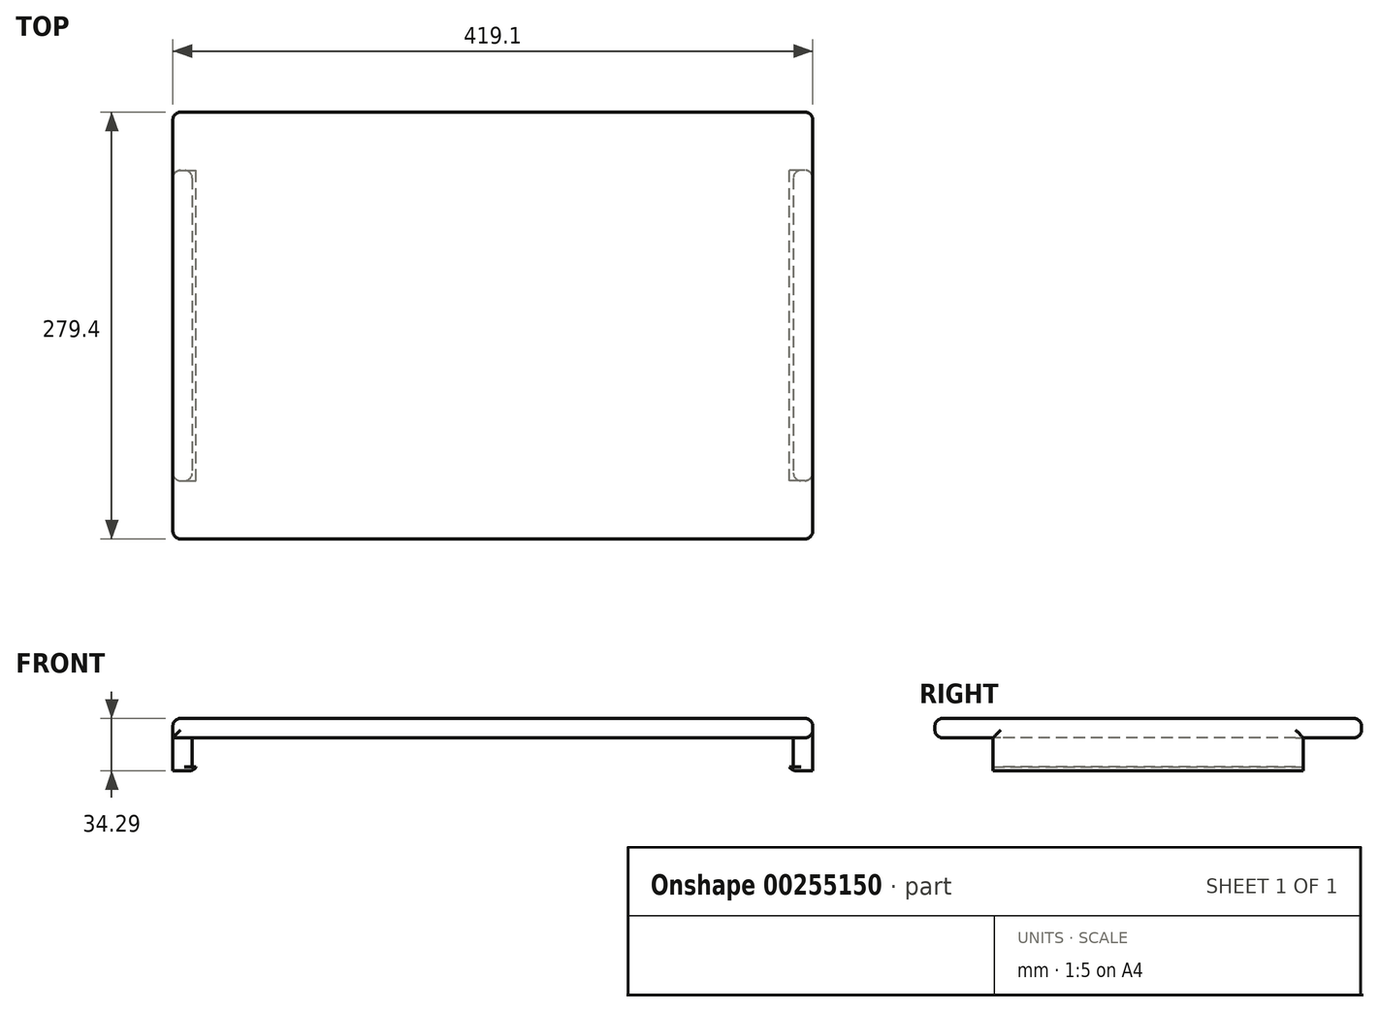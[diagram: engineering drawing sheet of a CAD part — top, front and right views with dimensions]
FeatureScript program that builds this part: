
annotation { "Feature Type Name" : "Feature", "Feature Type Description" : "" }
export const myFeature = defineFeature(function(context is Context, id is Id, definition is map)
    precondition{}
    {
        {
            var Q0;
            Q0=qCreatedBy(makeId("Top.planeOp"),FACE);
            var sketch = newSketch(context, id + "F0", { "sketchPlane" : qUnion([Q0])});
            skLineSegment(sketch, "E0.bottom", {"start": v(-209.55, 139.7) * mm, "end": v(209.55, 139.7) * mm});
            skLineSegment(sketch, "E0.top", {"start": v(-209.55, -139.7) * mm, "end": v(209.55, -139.7) * mm});
            skLineSegment(sketch, "E0.left", {"start": v(-209.55, 139.7) * mm, "end": v(-209.55, -139.7) * mm});
            skLineSegment(sketch, "E0.right", {"start": v(209.55, 139.7) * mm, "end": v(209.55, -139.7) * mm});
            skLineSegment(sketch, "E1.bottom", {"start": v(-209.55, 101.6) * mm, "end": v(-196.85, 101.6) * mm});
            skLineSegment(sketch, "E1.top", {"start": v(-209.55, -101.6) * mm, "end": v(-196.85, -101.6) * mm});
            skLineSegment(sketch, "E1.left", {"start": v(-209.55, 101.6) * mm, "end": v(-209.55, -101.6) * mm});
            skLineSegment(sketch, "E1.right", {"start": v(-196.85, 101.6) * mm, "end": v(-196.85, -101.6) * mm});
            skLineSegment(sketch, "E2.bottom", {"start": v(209.55, 101.6) * mm, "end": v(196.85, 101.6) * mm});
            skLineSegment(sketch, "E2.top", {"start": v(209.55, -101.6) * mm, "end": v(196.85, -101.6) * mm});
            skLineSegment(sketch, "E2.left", {"start": v(209.55, 101.6) * mm, "end": v(209.55, -101.6) * mm});
            skLineSegment(sketch, "E2.right", {"start": v(196.85, 101.6) * mm, "end": v(196.85, -101.6) * mm});
            skLineSegment(sketch, "E3.bottom", {"start": v(-76.2, -139.7) * mm, "end": v(76.2, -139.7) * mm});
            skLineSegment(sketch, "E3.top", {"start": v(-76.2, -127) * mm, "end": v(76.2, -127) * mm});
            skLineSegment(sketch, "E3.left", {"start": v(-76.2, -139.7) * mm, "end": v(-76.2, -127) * mm});
            skLineSegment(sketch, "E3.right", {"start": v(76.2, -139.7) * mm, "end": v(76.2, -127) * mm});
            skSolve(sketch);
        }
        {
            var Q0;
            Q0 = qSketchRegion(id + "F0", true);
            extrude(context, id + "F1", {"entities" : qUnion([Q0]), "depth" : 12.7 * mm});
        }
        {
            var Q0;
            Q0=makeQuery(id+"F0.imprint","IMPRINT",FACE,{"disambiguationData":[TD([[makeQuery(id+"F0.imprint","IMPRINT",EDGE,{"derivedFrom":sQuery(id+"F0.wireOp",EDGE,"E1.bottom")}),-1.0]])]});
            var Q1;
            Q1=makeQuery(id+"F0.imprint","IMPRINT",FACE,{"disambiguationData":[TD([[makeQuery(id+"F0.imprint","IMPRINT",EDGE,{"derivedFrom":sQuery(id+"F0.wireOp",EDGE,"E2.bottom")}),1.0]])]});
            var Q2;
            Q2=makeQuery(id+"F0.imprint","IMPRINT",FACE,{"disambiguationData":[TD([[makeQuery(id+"F0.imprint","IMPRINT",EDGE,{"derivedFrom":sQuery(id+"F0.wireOp",EDGE,"E3.bottom")}),1.0]])]});
            extrude(context, id + "F2", {"entities" : qUnion([Q0, Q1, Q2]), "operationType" : NewBodyOperationType.ADD, "oppositeDirection" : true, "depth" : 19.05 * mm});
        }
        {
            var Q0;
            Q0=makeQuery(id+"F1.opExtrude","SWEPT_EDGE",EDGE,{"disambiguationData":[OSD([sQuery(id+"F0.wireOp",EDGE,"E0.bottom"),sQuery(id+"F0.wireOp",EDGE,"E0.right")])]});
            var Q1;
            Q1=makeQuery(id+"F1.opExtrude","CAP_EDGE",EDGE,{"disambiguationData":[OSD([sQuery(id+"F0.wireOp",EDGE,"E0.right"),sQuery(id+"F0.wireOp",EDGE,"E2.left")])],"isStart":false});
            var Q2;
            Q2=makeQuery(id+"F1.opExtrude","CAP_EDGE",EDGE,{"disambiguationData":[OSD([sQuery(id+"F0.wireOp",EDGE,"E0.bottom")])],"isStart":false});
            var Q3;
            Q3=makeQuery(id+"F1.opExtrude","CAP_EDGE",EDGE,{"disambiguationData":[OSD([sQuery(id+"F0.wireOp",EDGE,"E0.bottom")])],"isStart":true});
            var Q4;
            {var subQ0=sQuery(id+"F0.wireOp",EDGE,"E2.left");var subQ1=sQuery(id+"F0.wireOp",EDGE,"E0.right");var subQ2=sQuery(id+"F0.wireOp",EDGE,"E0.bottom");Q4=makeQuery(id+"F2.boolean.opBoolean","SPLIT",EDGE,{"disambiguationData":[TD([makeQuery(id+"F1.opExtrude","SWEPT_FACE",FACE,{"disambiguationData":[OSD([subQ2])]})])],"derivedFrom":makeQuery(id+"F1.opExtrude","CAP_EDGE",EDGE,{"disambiguationData":[OSD([subQ1,subQ0])],"isStart":true})});}
            var Q5;
            {var subQ0=sQuery(id+"F0.wireOp",EDGE,"E2.left");var subQ1=sQuery(id+"F0.wireOp",EDGE,"E0.right");var subQ2=sQuery(id+"F0.wireOp",EDGE,"E0.top");Q5=makeQuery(id+"F2.boolean.opBoolean","SPLIT",EDGE,{"disambiguationData":[TD([makeQuery(id+"F1.opExtrude","SWEPT_FACE",FACE,{"disambiguationData":[OSD([subQ2])]})])],"derivedFrom":makeQuery(id+"F1.opExtrude","CAP_EDGE",EDGE,{"disambiguationData":[OSD([subQ1,subQ0])],"isStart":true})});}
            var Q6;
            Q6=makeQuery(id+"F1.opExtrude","CAP_EDGE",EDGE,{"disambiguationData":[OSD([sQuery(id+"F0.wireOp",EDGE,"E0.top")])],"isStart":true});
            var Q7;
            Q7=makeQuery(id+"F1.opExtrude","CAP_EDGE",EDGE,{"disambiguationData":[OSD([sQuery(id+"F0.wireOp",EDGE,"E0.top")])],"isStart":false});
            var Q8;
            Q8=makeQuery(id+"F1.opExtrude","SWEPT_EDGE",EDGE,{"disambiguationData":[OSD([sQuery(id+"F0.wireOp",EDGE,"E0.top"),sQuery(id+"F0.wireOp",EDGE,"E0.right")])]});
            var Q9;
            Q9=makeQuery(id+"F1.opExtrude","SWEPT_EDGE",EDGE,{"disambiguationData":[OSD([sQuery(id+"F0.wireOp",EDGE,"E0.top"),sQuery(id+"F0.wireOp",EDGE,"E0.left")])]});
            var Q10;
            Q10=makeQuery(id+"F2.opExtrude","SWEPT_EDGE",EDGE,{"disambiguationData":[OSD([sQuery(id+"F0.wireOp",EDGE,"E0.left"),sQuery(id+"F0.wireOp",EDGE,"E1.top"),sQuery(id+"F0.wireOp",EDGE,"E1.left")])]});
            var Q11;
            Q11=makeQuery(id+"F2.opExtrude","SWEPT_EDGE",EDGE,{"disambiguationData":[OSD([sQuery(id+"F0.wireOp",EDGE,"E0.left"),sQuery(id+"F0.wireOp",EDGE,"E1.bottom"),sQuery(id+"F0.wireOp",EDGE,"E1.left")])]});
            var Q12;
            Q12=makeQuery(id+"F2.opExtrude","SWEPT_EDGE",EDGE,{"disambiguationData":[OSD([sQuery(id+"F0.wireOp",EDGE,"E2.bottom"),sQuery(id+"F0.wireOp",EDGE,"E2.right")])]});
            var Q13;
            Q13=makeQuery(id+"F2.opExtrude","SWEPT_EDGE",EDGE,{"disambiguationData":[OSD([sQuery(id+"F0.wireOp",EDGE,"E0.right"),sQuery(id+"F0.wireOp",EDGE,"E2.bottom"),sQuery(id+"F0.wireOp",EDGE,"E2.left")])]});
            var Q14;
            {var subQ0=sQuery(id+"F0.wireOp",EDGE,"E1.left");var subQ1=sQuery(id+"F0.wireOp",EDGE,"E0.left");var subQ2=sQuery(id+"F0.wireOp",EDGE,"E0.bottom");Q14=makeQuery(id+"F2.boolean.opBoolean","SPLIT",EDGE,{"disambiguationData":[TD([makeQuery(id+"F1.opExtrude","SWEPT_FACE",FACE,{"disambiguationData":[OSD([subQ2])]})])],"derivedFrom":makeQuery(id+"F1.opExtrude","CAP_EDGE",EDGE,{"disambiguationData":[OSD([subQ1,subQ0])],"isStart":true})});}
            var Q15;
            Q15=makeQuery(id+"F2.opExtrude","CAP_EDGE",EDGE,{"disambiguationData":[OSD([sQuery(id+"F0.wireOp",EDGE,"E1.right")])],"isStart":true});
            var Q16;
            Q16=makeQuery(id+"F2.opExtrude","CAP_EDGE",EDGE,{"disambiguationData":[OSD([sQuery(id+"F0.wireOp",EDGE,"E2.right")])],"isStart":true});
            var Q17;
            Q17=makeQuery(id+"F2.opExtrude","CAP_EDGE",EDGE,{"disambiguationData":[OSD([sQuery(id+"F0.wireOp",EDGE,"E1.bottom")])],"isStart":true});
            var Q18;
            Q18=makeQuery(id+"F2.opExtrude","SWEPT_EDGE",EDGE,{"disambiguationData":[OSD([sQuery(id+"F0.wireOp",EDGE,"E1.bottom"),sQuery(id+"F0.wireOp",EDGE,"E1.right")])]});
            var Q19;
            Q19=makeQuery(id+"F1.opExtrude","CAP_EDGE",EDGE,{"disambiguationData":[OSD([sQuery(id+"F0.wireOp",EDGE,"E0.left"),sQuery(id+"F0.wireOp",EDGE,"E1.left")])],"isStart":false});
            var Q20;
            Q20=makeQuery(id+"F1.opExtrude","SWEPT_EDGE",EDGE,{"disambiguationData":[OSD([sQuery(id+"F0.wireOp",EDGE,"E0.bottom"),sQuery(id+"F0.wireOp",EDGE,"E0.left")])]});
            var Q21;
            Q21=makeQuery(id+"F2.opExtrude","SWEPT_EDGE",EDGE,{"disambiguationData":[OSD([sQuery(id+"F0.wireOp",EDGE,"E2.top"),sQuery(id+"F0.wireOp",EDGE,"E2.right")])]});
            var Q22;
            Q22=makeQuery(id+"F2.opExtrude","SWEPT_EDGE",EDGE,{"disambiguationData":[OSD([sQuery(id+"F0.wireOp",EDGE,"E0.right"),sQuery(id+"F0.wireOp",EDGE,"E2.top"),sQuery(id+"F0.wireOp",EDGE,"E2.left")])]});
            var Q23;
            Q23=makeQuery(id+"F2.opExtrude","SWEPT_EDGE",EDGE,{"disambiguationData":[OSD([sQuery(id+"F0.wireOp",EDGE,"E1.top"),sQuery(id+"F0.wireOp",EDGE,"E1.right")])]});
            var Q24;
            Q24=makeQuery(id+"F2.opExtrude","SWEPT_EDGE",EDGE,{"disambiguationData":[OSD([sQuery(id+"F0.wireOp",EDGE,"E3.top"),sQuery(id+"F0.wireOp",EDGE,"E3.left")])]});
            var Q25;
            Q25=makeQuery(id+"F2.opExtrude","SWEPT_EDGE",EDGE,{"disambiguationData":[OSD([sQuery(id+"F0.wireOp",EDGE,"E3.top"),sQuery(id+"F0.wireOp",EDGE,"E3.right")])]});
            var Q26;
            Q26=makeQuery(id+"F2.opExtrude","CAP_EDGE",EDGE,{"disambiguationData":[OSD([sQuery(id+"F0.wireOp",EDGE,"E3.top")])],"isStart":false});
            var Q27;
            Q27=makeQuery(id+"F2.opExtrude","CAP_EDGE",EDGE,{"disambiguationData":[OSD([sQuery(id+"F0.wireOp",EDGE,"E3.bottom")])],"isStart":false});
            var Q28;
            Q28=makeQuery(id+"F2.opExtrude","CAP_EDGE",EDGE,{"disambiguationData":[OSD([sQuery(id+"F0.wireOp",EDGE,"E3.left")])],"isStart":false});
            var Q29;
            Q29=makeQuery(id+"F2.opExtrude","CAP_EDGE",EDGE,{"disambiguationData":[OSD([sQuery(id+"F0.wireOp",EDGE,"E3.right")])],"isStart":false});
            var Q30;
            Q30=makeQuery(id+"F2.opExtrude","SWEPT_EDGE",EDGE,{"disambiguationData":[OSD([sQuery(id+"F0.wireOp",EDGE,"E0.top"),sQuery(id+"F0.wireOp",EDGE,"E3.bottom"),sQuery(id+"F0.wireOp",EDGE,"E3.left")])]});
            var Q31;
            Q31=makeQuery(id+"F2.opExtrude","SWEPT_EDGE",EDGE,{"disambiguationData":[OSD([sQuery(id+"F0.wireOp",EDGE,"E0.top"),sQuery(id+"F0.wireOp",EDGE,"E3.bottom"),sQuery(id+"F0.wireOp",EDGE,"E3.right")])]});
            var Q32;
            Q32=makeQuery(id+"F2.opExtrude","CAP_EDGE",EDGE,{"disambiguationData":[OSD([sQuery(id+"F0.wireOp",EDGE,"E3.top")])],"isStart":true});
            fillet(context, id + "F3", {"entities" : qUnion([Q0, Q1, Q2, Q3, Q4, Q5, Q6, Q7, Q8, Q9, Q10, Q11, Q12, Q13, Q14, Q15, Q16, Q17, Q18, Q19, Q20, Q21, Q22, Q23, Q24, Q25, Q26, Q27, Q28, Q29, Q30, Q31, Q32]), "radius" : 5.08 * mm, "tangentPropagation" : true, "allowEdgeOverflow" : false});
        }
        {
            var Q0;
            Q0=makeQuery(id+"F2.opExtrude","CAP_FACE",FACE,{"disambiguationData":[OSD([sQuery(id+"F0.wireOp",EDGE,"E1.bottom"),sQuery(id+"F0.wireOp",EDGE,"E1.top"),sQuery(id+"F0.wireOp",EDGE,"E1.left"),sQuery(id+"F0.wireOp",EDGE,"E1.right")])],"isStart":false});
            var sketch = newSketch(context, id + "F4", { "sketchPlane" : qUnion([Q0])});
            skLineSegment(sketch, "E4.bottom", {"start": v(-209.55, 101.6) * mm, "end": v(-194.3, 101.6) * mm});
            skLineSegment(sketch, "E4.top", {"start": v(-209.55, -101.6) * mm, "end": v(-194.3, -101.6) * mm});
            skLineSegment(sketch, "E4.left", {"start": v(-209.55, 101.6) * mm, "end": v(-209.55, -101.6) * mm});
            skLineSegment(sketch, "E4.right", {"start": v(-194.3, 101.6) * mm, "end": v(-194.3, -101.6) * mm});
            skLineSegment(sketch, "E5.bottom", {"start": v(209.55, 101.6) * mm, "end": v(194.3, 101.6) * mm});
            skLineSegment(sketch, "E5.top", {"start": v(209.55, -101.6) * mm, "end": v(194.31, -101.6) * mm});
            skLineSegment(sketch, "E5.left", {"start": v(209.55, 101.6) * mm, "end": v(209.55, -101.6) * mm});
            skLineSegment(sketch, "E5.right", {"start": v(194.3, 101.6) * mm, "end": v(194.31, -101.6) * mm});
            skSolve(sketch);
        }
        {
            var Q0;
            Q0 = qSketchRegion(id + "F4", true);
            extrude(context, id + "F5", {"entities" : qUnion([Q0]), "operationType" : NewBodyOperationType.ADD, "depth" : 2.54 * mm});
        }
        {
            var Q0;
            Q0=makeQuery(id+"F5.opExtrude","CAP_EDGE",EDGE,{"disambiguationData":[OSD([sQuery(id+"F4.wireOp",EDGE,"E4.right")])],"isStart":false});
            var Q1;
            Q1=makeQuery(id+"F5.opExtrude","CAP_EDGE",EDGE,{"disambiguationData":[OSD([sQuery(id+"F4.wireOp",EDGE,"E5.right")])],"isStart":false});
            fillet(context, id + "F6", {"entities" : qUnion([Q0, Q1]), "radius" : 5.08 * mm, "tangentPropagation" : true, "allowEdgeOverflow" : false});
        }
        {
            var Q0;
            Q0=makeQuery(id+"F5.opExtrude","SWEPT_EDGE",EDGE,{"disambiguationData":[OSD([sQuery(id+"F4.wireOp",EDGE,"E4.bottom"),sQuery(id+"F4.wireOp",EDGE,"E4.left")])]});
            var Q1;
            Q1=makeQuery(id+"F5.opExtrude","SWEPT_EDGE",EDGE,{"disambiguationData":[OSD([sQuery(id+"F4.wireOp",EDGE,"E5.bottom"),sQuery(id+"F4.wireOp",EDGE,"E5.left")])]});
            var Q2;
            Q2=makeQuery(id+"F5.opExtrude","SWEPT_EDGE",EDGE,{"disambiguationData":[OSD([sQuery(id+"F4.wireOp",EDGE,"E5.top"),sQuery(id+"F4.wireOp",EDGE,"E5.left")])]});
            var Q3;
            Q3=makeQuery(id+"F5.opExtrude","SWEPT_EDGE",EDGE,{"disambiguationData":[OSD([sQuery(id+"F4.wireOp",EDGE,"E4.top"),sQuery(id+"F4.wireOp",EDGE,"E4.left")])]});
            fillet(context, id + "F7", {"entities" : qUnion([Q0, Q1, Q2, Q3]), "radius" : 5.08 * mm, "tangentPropagation" : true, "allowEdgeOverflow" : false});
        }
    });
